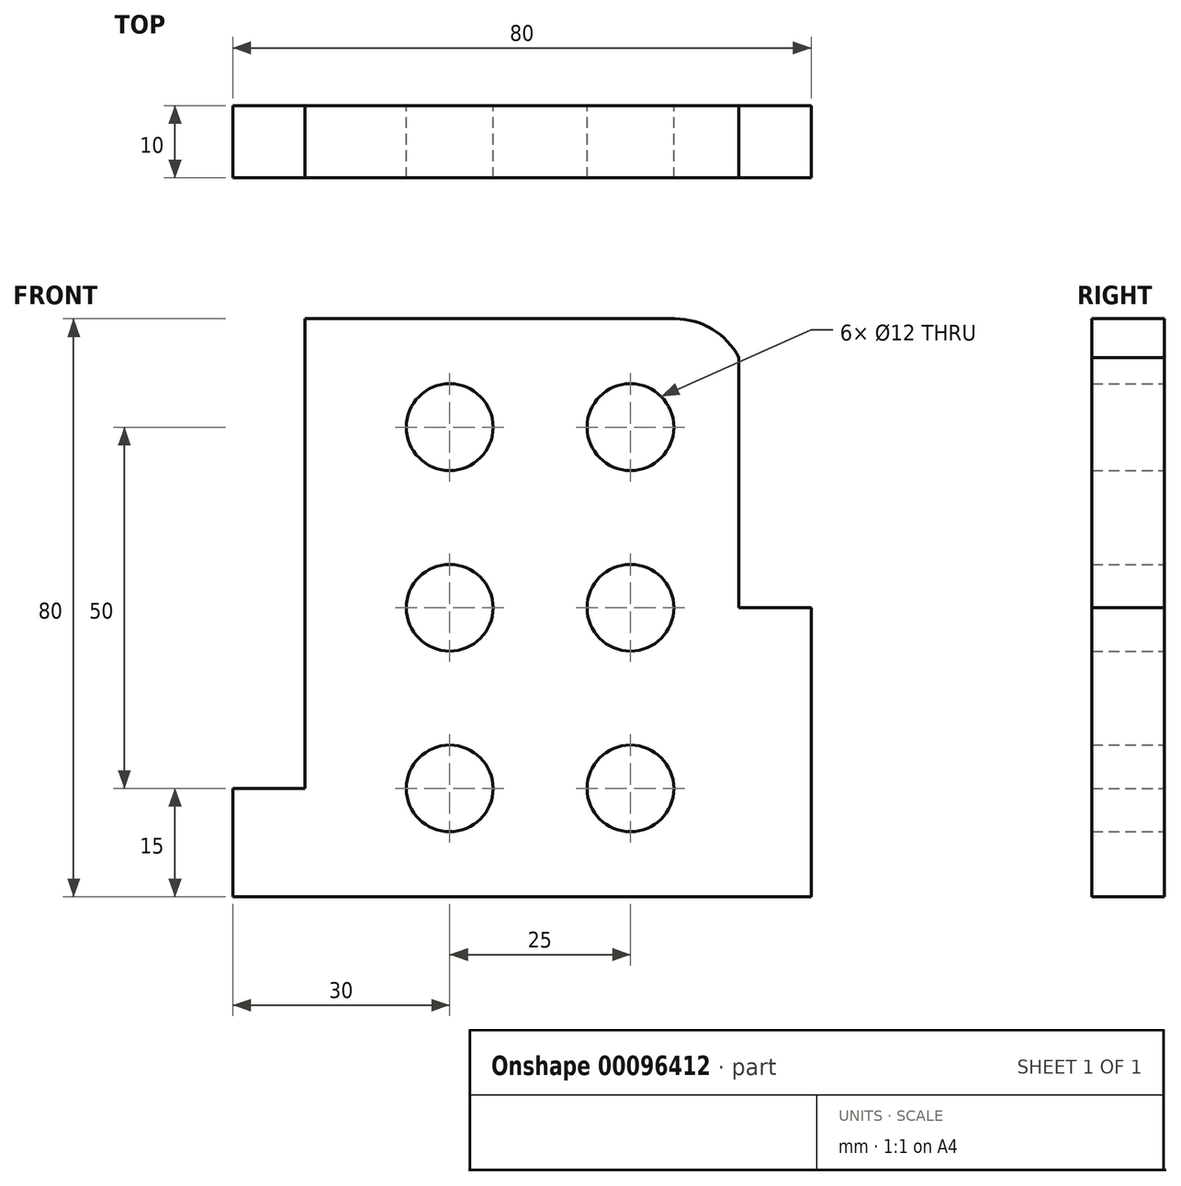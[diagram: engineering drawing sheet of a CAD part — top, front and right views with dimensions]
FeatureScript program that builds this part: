
annotation { "Feature Type Name" : "Feature", "Feature Type Description" : "" }
export const myFeature = defineFeature(function(context is Context, id is Id, definition is map)
    precondition{}
    {
        {
            var Q0;
            Q0=qCreatedBy(makeId("Front.planeOp"),FACE);
            var sketch = newSketch(context, id + "F0", { "sketchPlane" : qUnion([Q0])});
            skLineSegment(sketch, "E0", {"start": v(0, 0) * mm, "end": v(80, 0) * mm});
            skLineSegment(sketch, "E1", {"start": v(80, 0) * mm, "end": v(80, 40) * mm});
            skLineSegment(sketch, "E2", {"start": v(80, 40) * mm, "end": v(70, 40) * mm});
            skLineSegment(sketch, "E3", {"start": v(70, 40) * mm, "end": v(70, 74.64) * mm});
            skLineSegment(sketch, "E4", {"start": v(0, 0) * mm, "end": v(0, 15) * mm});
            skLineSegment(sketch, "E5", {"start": v(0, 15) * mm, "end": v(10, 15) * mm});
            skLineSegment(sketch, "E6", {"start": v(10, 15) * mm, "end": v(10, 80) * mm});
            skLineSegment(sketch, "E7", {"start": v(10, 80) * mm, "end": v(61.14, 80) * mm});
            skArc(sketch, "E8", {"start": v(70, 74.64) * mm, "mid": v(66.32, 78.56) * mm, "end": v(61.14, 80) * mm});
            skCircle(sketch, "E9", {"center": v(30, 15) * mm, "radius": 6 * mm});
            skCircle(sketch, "E10", {"center": v(55, 15) * mm, "radius": 6 * mm});
            skCircle(sketch, "E11", {"center": v(30, 40) * mm, "radius": 6 * mm});
            skCircle(sketch, "E12", {"center": v(55, 40) * mm, "radius": 6 * mm});
            skCircle(sketch, "E13", {"center": v(30, 65) * mm, "radius": 6 * mm});
            skCircle(sketch, "E14", {"center": v(55, 65) * mm, "radius": 6 * mm});
            skSolve(sketch);
        }
        {
            var Q0;
            Q0=makeQuery(id+"F0.imprint","IMPRINT",FACE,{"disambiguationData":[TD([[makeQuery(id+"F0.imprint","IMPRINT",EDGE,{"derivedFrom":sQuery(id+"F0.wireOp",EDGE,"E0")}),1.0]])]});
            extrude(context, id + "F1", {"entities" : qUnion([Q0]), "depth" : 10 * mm});
        }
    });
